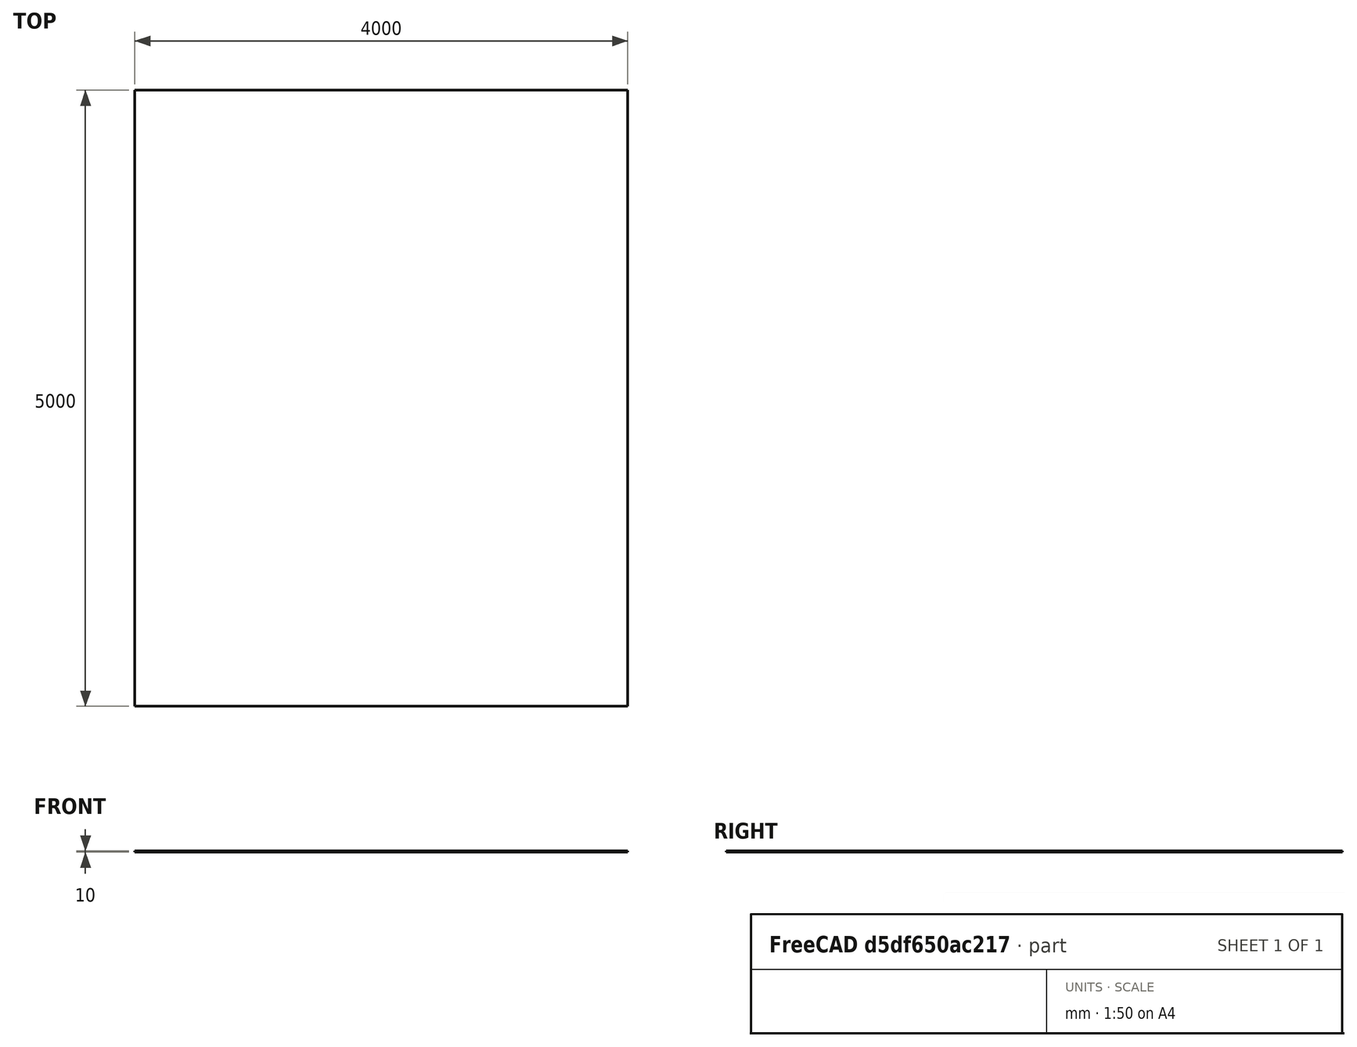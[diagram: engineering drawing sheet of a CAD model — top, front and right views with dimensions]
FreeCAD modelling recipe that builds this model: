
FCSTD DOCUMENT  (FreeCAD 0.21R33694 (Git))
Label: SteelPlate
License: All rights reserved
LicenseURL: https://en.wikipedia.org/wiki/All_rights_reserved
objects: Part::Box×1, App::MaterialObjectPython×1, Fem::ConstraintPressure×1, Fem::FemSolverObjectPython×1, Fem::ConstraintFixed×1, Fem::FemMeshObjectPython×1, Fem::FemAnalysis×1
note: 1 computed .brp shape members not serialized (recipe doc carries the construction recipe); baked Part::Feature solids carry a one-line shape summary decoded from their .brp

FEATURE [Part::Box] Box  label="Würfel"
  AttacherType = Attacher::AttachEngine3D
  Height = 10
  Length = 4000
  Width = 5000
FEATURE [App::MaterialObjectPython] MaterialSolid  # material (typed FeaturePython)
  Category = 0
  Material = AuthorAndLicense=(c) 2013 Juergen Riegel (CC-BY 3.0),CardName=Steel-JLU,Density=7870.0 kg/m^3,+9 more (map truncated)
FEATURE [Fem::ConstraintPressure] ConstraintPressure
  NormalDirection = (0,0,-1)
  Normals = (72) [(0,0,-1),(0,0,-1),(0,0,-1),(0,0,-1),(0,0,-1),(0,0,-1),(0,0,-1),(0,0,-1),(0,0,-1),(0,0,-1),(0,0,-1),(0,0,-1),(0,0,-1),(0,0,-1),(0,0,-1),(0,0,-1),+56 more]
  Points = (72) [(0,0,0),(571.429,0,0),(1142.86,0,0),(1714.29,0,0),(2285.71,0,0),(2857.14,0,0),(3428.57,0,0),(4000,0,0),(0,625,0),(571.429,625,0),(1142.86,625,0),+61 more]
  Pressure = 0.001
  References = -> [Box]
  Scale = 60
FEATURE [Fem::FemSolverObjectPython] SolverCcxTools  # FEM object (typed FeaturePython)
  AnalysisType = 0
  BeamShellResultOutput3D = true
  BucklingFactors = 1
  EigenmodeHighLimit = 1000000
  EigenmodeLowLimit = 0
  EigenmodesCount = 10
  GeometricalNonlinearity = 0
  IterationsControlParameterCutb = 0.25,0.5,0.75,0.85,,,1.5,
  IterationsControlParameterIter = 4,8,9,200,10,400,,200,,
  IterationsControlParameterTimeUse = false
  IterationsThermoMechMaximum = 2000
  IterationsUserDefinedIncrementations = false
  IterationsUserDefinedTimeStepLength = false
  MaterialNonlinearity = 0
  MatrixSolverType = 0
  SplitInputWriter = false
  ThermoMechSteadyState = true
  TimeEnd = 1
  TimeInitialStep = 0.01
FEATURE [Fem::ConstraintFixed] ConstraintFixed
  NormalDirection = (0,1,0)
  Normals = (126) [(0,1,0),(0,1,0),(0,1,0),(0,1,0),(0,1,0),(0,1,0),(0,1,0),(0,1,0),(0,1,0),(0,1,0),(0,1,0),(0,1,0),(0,1,0),(0,1,0),(0,1,0),(0,1,0),(0,1,0),(0,1,0),+108 more]
  Points = (126) [(0,5000,0),(0,5000,5),(0,5000,10),(444.444,5000,0),(444.444,5000,5),(444.444,5000,10),(888.889,5000,0),(888.889,5000,5),(888.889,5000,10),+117 more]
  References = -> [Box]
FEATURE [Fem::FemMeshObjectPython] FEMMeshGmsh  # FEM object (typed FeaturePython)
  Algorithm2D = 0
  Algorithm3D = 0
  CharacteristicLengthMax = 100
  CharacteristicLengthMin = 0
  CoherenceMesh = true
  ElementDimension = 0
  ElementOrder = 1
  GeometryTolerance = 1e-06
  GroupsOfNodes = false
  HighOrderOptimize = 0
  MeshSizeFromCurvature = 12
  OptimizeNetgen = false
  OptimizeStd = true
  Part = -> Box
  RecombinationAlgorithm = 0
  Recombine3DAll = false
  RecombineAll = false
  SecondOrderLinear = false
FEATURE [Fem::FemAnalysis] Analysis
  Group = -> [MaterialSolid,ConstraintPressure,SolverCcxTools,ConstraintFixed,FEMMeshGmsh]
